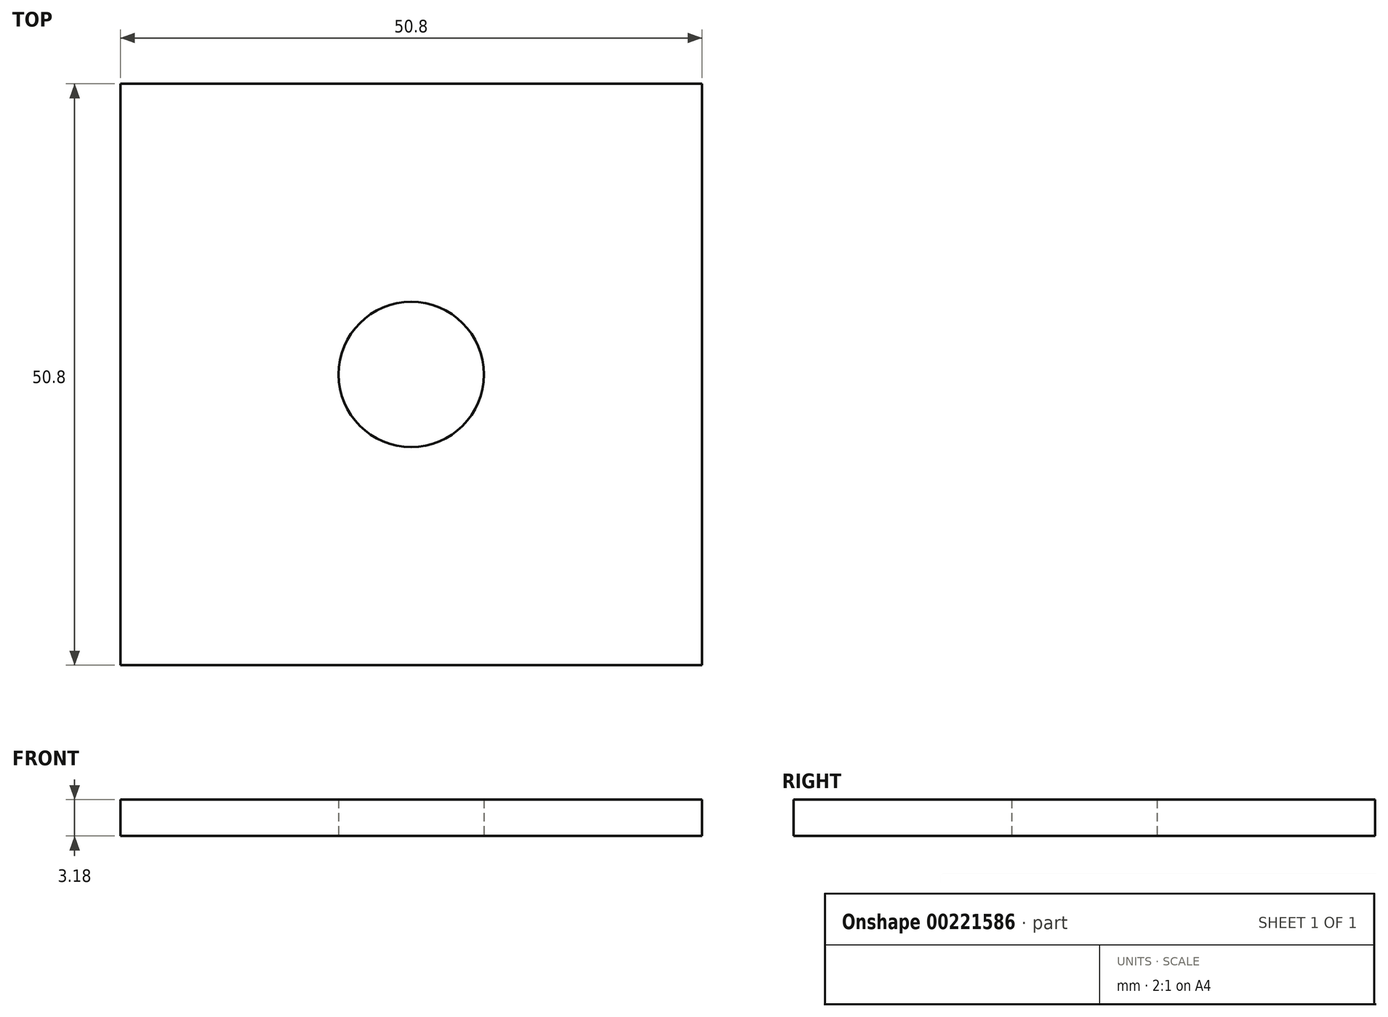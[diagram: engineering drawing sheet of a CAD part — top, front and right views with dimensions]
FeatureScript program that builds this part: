
annotation { "Feature Type Name" : "Feature", "Feature Type Description" : "" }
export const myFeature = defineFeature(function(context is Context, id is Id, definition is map)
    precondition{}
    {
        {
            var Q0;
            Q0=qCreatedBy(makeId("Top.planeOp"),FACE);
            var sketch = newSketch(context, id + "F0", { "sketchPlane" : qUnion([Q0])});
            skLineSegment(sketch, "E0.bottom", {"start": v(25.4, 25.4) * mm, "end": v(-25.4, 25.4) * mm});
            skLineSegment(sketch, "E0.top", {"start": v(25.4, -25.4) * mm, "end": v(-25.4, -25.4) * mm});
            skLineSegment(sketch, "E0.left", {"start": v(25.4, 25.4) * mm, "end": v(25.4, -25.4) * mm});
            skLineSegment(sketch, "E0.right", {"start": v(-25.4, 25.4) * mm, "end": v(-25.4, -25.4) * mm});
            skPoint(sketch, "E0.middle", {"position": v(0, 0) * mm});
            skSolve(sketch);
        }
        {
            var Q0;
            Q0=makeQuery(id+"F0.imprint","IMPRINT",FACE,{"disambiguationData":[TD([[makeQuery(id+"F0.imprint","IMPRINT",EDGE,{"derivedFrom":sQuery(id+"F0.wireOp",EDGE,"E0.bottom")}),1.0]])]});
            extrude(context, id + "F1", {"entities" : qUnion([Q0]), "depth" : 3.17 * mm});
        }
        {
            var Q0;
            Q0=qCreatedBy(makeId("Top.planeOp"),FACE);
            var sketch = newSketch(context, id + "F2", { "sketchPlane" : qUnion([Q0])});
            skCircle(sketch, "E1", {"center": v(0, 0) * mm, "radius": 6.35 * mm});
            skSolve(sketch);
        }
        {
            var Q0;
            Q0=makeQuery(id+"F2.imprint","IMPRINT",FACE,{"disambiguationData":[TD([[makeQuery(id+"F2.imprint","IMPRINT",EDGE,{"derivedFrom":sQuery(id+"F2.wireOp",EDGE,"E1")}),1.0]])]});
            extrude(context, id + "F3", {"entities" : qUnion([Q0]), "depth" : 3.17 * mm});
        }
    });
